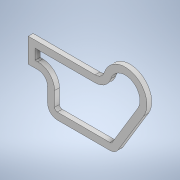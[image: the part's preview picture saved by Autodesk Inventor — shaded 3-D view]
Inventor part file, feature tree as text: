
AUTODESK INVENTOR PART (.ipt)
format: ipt  version: 2020 (Build 240168000, 168)  size: 159,232 bytes
history: native  units: mm
features: extrude x2, sketch x2, projected_geometry x1
ambient origin geometry x8: Origin, YZ Plane, XZ Plane, XY Plane, X Axis, Y Axis, Z Axis, Center Point
bodies: Solid1 (feature_tree)
feature tree (5):
  extrude  "Extrusion1"  Depth=40.0mm
  extrude  "Extrusion3"  Depth=20.0mm
  sketch  "Sketch1"  dims[d2=200.0mm d3=40.0mm]
  sketch  "Sketch3"  dims[d4=50.0mm d5=20.0mm d6=40.0mm d7=90.0mm d8=180.0mm d9=120.0mm d10=10.0mm d11=0.0mm d15=0.0mm d16=0.0mm]
  projected_geometry  "Projected Loop3"
